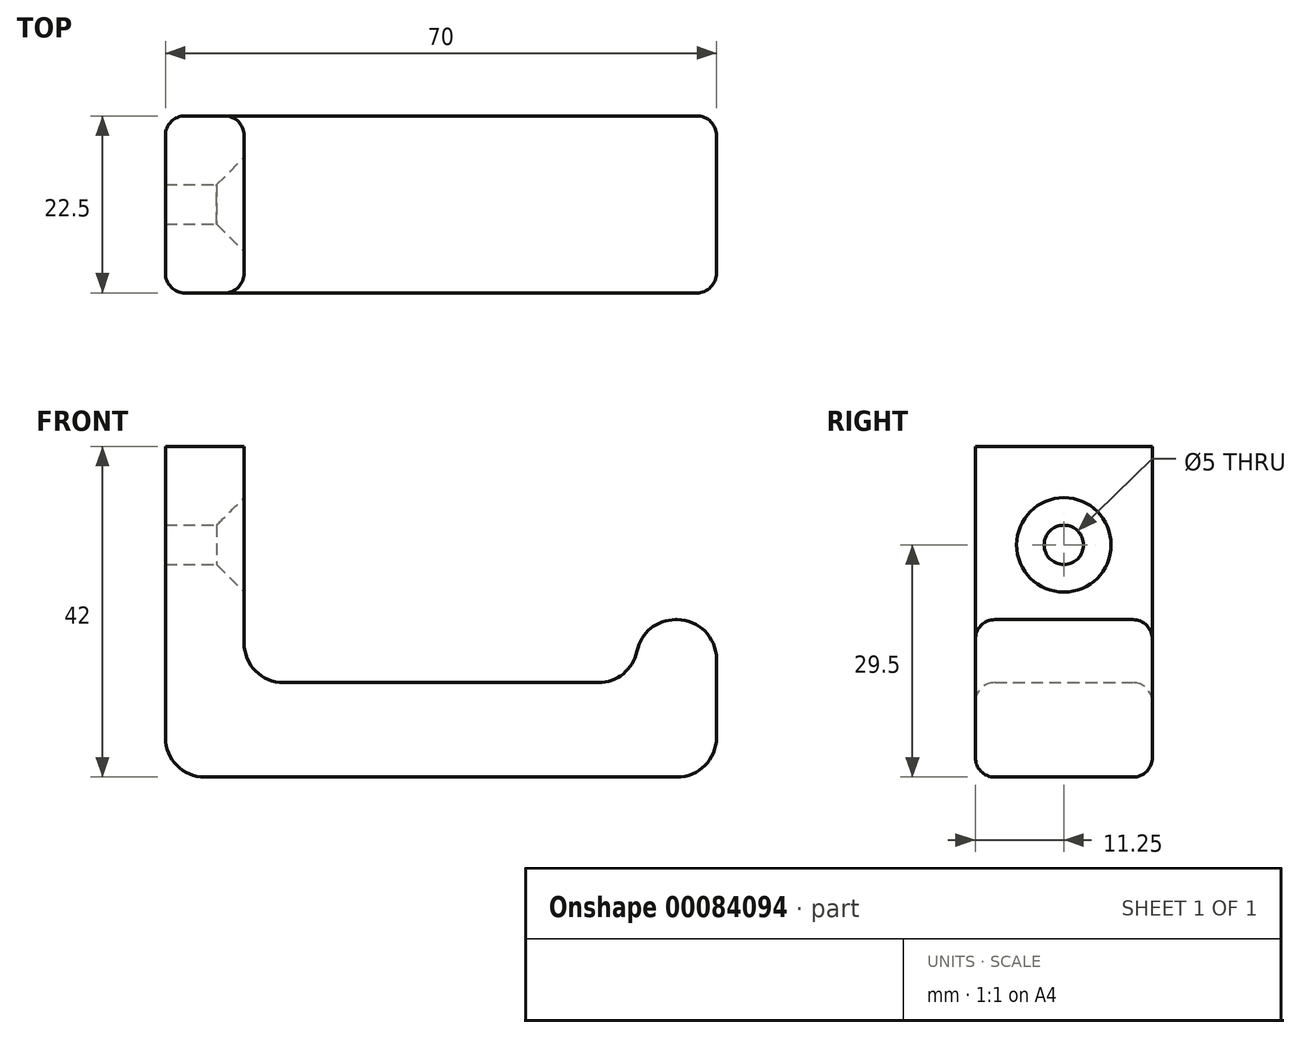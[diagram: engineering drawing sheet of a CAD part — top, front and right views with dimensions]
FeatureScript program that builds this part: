
annotation { "Feature Type Name" : "Feature", "Feature Type Description" : "" }
export const myFeature = defineFeature(function(context is Context, id is Id, definition is map)
    precondition{}
    {
        {
            var Q0;
            Q0=qCreatedBy(makeId("Front.planeOp"),FACE);
            var sketch = newSketch(context, id + "F0", { "sketchPlane" : qUnion([Q0])});
            skLineSegment(sketch, "E0", {"start": v(0, 5) * mm, "end": v(0, 42) * mm});
            skLineSegment(sketch, "E1", {"start": v(0, 42) * mm, "end": v(10, 42) * mm});
            skLineSegment(sketch, "E2", {"start": v(10, 42) * mm, "end": v(10, 17) * mm});
            skLineSegment(sketch, "E3", {"start": v(15, 12) * mm, "end": v(55, 12) * mm});
            skLineSegment(sketch, "E4", {"start": v(60, 17) * mm, "end": v(60, 20) * mm});
            skLineSegment(sketch, "E5", {"start": v(60, 20) * mm, "end": v(70, 20) * mm});
            skLineSegment(sketch, "E6", {"start": v(70, 20) * mm, "end": v(70, 5) * mm});
            skLineSegment(sketch, "E7", {"start": v(65, 0) * mm, "end": v(5, 0) * mm});
            skPoint(sketch, "E8.visualSharp", {"position": v(10, 12) * mm});
            skArc(sketch, "E8.filletArc", {"start": v(10, 17) * mm, "mid": v(11.46, 13.46) * mm, "end": v(15, 12) * mm});
            skPoint(sketch, "E9.visualSharp", {"position": v(60, 12) * mm});
            skArc(sketch, "E9.filletArc", {"start": v(55, 12) * mm, "mid": v(58.54, 13.46) * mm, "end": v(60, 17) * mm});
            skPoint(sketch, "E10.visualSharp", {"position": v(70, 0) * mm});
            skArc(sketch, "E10.filletArc", {"start": v(65, 0) * mm, "mid": v(68.54, 1.46) * mm, "end": v(70, 5) * mm});
            skPoint(sketch, "E11.visualSharp", {"position": v(0, 0) * mm});
            skArc(sketch, "E11.filletArc", {"start": v(0, 5) * mm, "mid": v(1.46, 1.46) * mm, "end": v(5, 0) * mm});
            skSolve(sketch);
        }
        {
            var Q0;
            Q0 = qSketchRegion(id + "F0", true);
            extrude(context, id + "F1", {"entities" : qUnion([Q0]), "depth" : 22.5 * mm});
        }
        {
            var Q0;
            Q0=makeQuery(id+"F1.opExtrude","SWEPT_FACE",FACE,{"disambiguationData":[OSD([sQuery(id+"F0.wireOp",EDGE,"E2")])]});
            var sketch = newSketch(context, id + "F2", { "sketchPlane" : qUnion([Q0])});
            skLineSegment(sketch, "E12", {"start": v(-22.5, 42) * mm, "end": v(0, 42) * mm});
            skLineSegment(sketch, "E13", {"start": v(-11.25, 42) * mm, "end": v(-11.25, 17) * mm});
            skPoint(sketch, "E13.endSnap0", {"position": v(-11.25, 42) * mm});
            skCircle(sketch, "E14", {"center": v(-11.25, 29.5) * mm, "radius": 2.5 * mm});
            skSolve(sketch);
        }
        {
            var Q0;
            {var subQ0=sQuery(id+"F2.wireOp",EDGE,"E14");var subQ1=sQuery(id+"F2.wireOp",EDGE,"E13");var subQ2=makeQuery(id+"F2.imprint","INTERSECT",VERTEX,{"disambiguationData":[OD(0.0)],"derivedFrom":[subQ1,subQ0]});Q0=makeQuery(id+"F2.imprint","IMPRINT",FACE,{"disambiguationData":[TD([[makeQuery(id+"F2.imprint","IMPRINT",EDGE,{"disambiguationData":[TD([[subQ2,-1.0]])],"derivedFrom":subQ1}),1.0]])]});}
            var Q1;
            {var subQ0=sQuery(id+"F2.wireOp",EDGE,"E14");var subQ1=sQuery(id+"F2.wireOp",EDGE,"E13");var subQ2=makeQuery(id+"F2.imprint","INTERSECT",VERTEX,{"disambiguationData":[OD(0.0)],"derivedFrom":[subQ1,subQ0]});Q1=makeQuery(id+"F2.imprint","IMPRINT",FACE,{"disambiguationData":[TD([[makeQuery(id+"F2.imprint","IMPRINT",EDGE,{"disambiguationData":[TD([[subQ2,-1.0]])],"derivedFrom":subQ1}),-1.0]])]});}
            extrude(context, id + "F3", {"entities" : qUnion([Q0, Q1]), "operationType" : NewBodyOperationType.REMOVE, "oppositeDirection" : true, "depth" : 25 * mm});
        }
        {
            var Q0;
            Q0=sQuery(id+"F2.wireOp",EDGE,"E13");
            cPlane(context, id + "F4", {"entities" : qUnion([Q0]), "cplaneType" : CPlaneType.LINE_ANGLE, "offset" : 150 * mm, "angle" : 90 * degree, "width" : 150 * mm, "height" : 150 * mm});
        }
        {
            var Q0;
            Q0=qCreatedBy(id+"F4.planeOp",FACE);
            var sketch = newSketch(context, id + "F5", { "sketchPlane" : qUnion([Q0])});
            skLineSegment(sketch, "E15", {"start": v(0, 42) * mm, "end": v(-10, 42) * mm});
            skLineSegment(sketch, "E16", {"start": v(-10, 42) * mm, "end": v(-10, 32) * mm});
            skLineSegment(sketch, "E17", {"start": v(-10, 32) * mm, "end": v(-6.5, 32) * mm});
            skLineSegment(sketch, "E18", {"start": v(-6.5, 32) * mm, "end": v(-10, 35.5) * mm});
            skLineSegment(sketch, "E19", {"start": v(-10, 29.5) * mm, "end": v(0, 29.5) * mm});
            skSolve(sketch);
        }
        {
            var Q0;
            Q0 = qSketchRegion(id + "F5", true);
            var Q1;
            Q1=sQuery(id+"F5.wireOp",EDGE,"E19");
            revolve(context, id + "F6", {"operationType" : NewBodyOperationType.REMOVE, "entities" : qUnion([Q0]), "axis" : qUnion([Q1]), "revolveType" : RevolveType.FULL, "oppositeDirection" : true});
        }
        {
            var Q0;
            Q0=makeQuery(id+"F1.opExtrude","SWEPT_EDGE",EDGE,{"disambiguationData":[OSD([sQuery(id+"F0.wireOp",EDGE,"E4"),sQuery(id+"F0.wireOp",EDGE,"E5")])]});
            fillet(context, id + "F7", {"entities" : qUnion([Q0]), "radius" : 5 * mm, "tangentPropagation" : true, "allowEdgeOverflow" : false});
        }
        {
            var Q0;
            Q0=makeQuery(id+"F1.opExtrude","SWEPT_EDGE",EDGE,{"disambiguationData":[OSD([sQuery(id+"F0.wireOp",EDGE,"E5"),sQuery(id+"F0.wireOp",EDGE,"E6")])]});
            fillet(context, id + "F8", {"entities" : qUnion([Q0]), "radius" : 5 * mm, "tangentPropagation" : true, "allowEdgeOverflow" : false});
        }
        {
            var Q0;
            Q0=makeQuery(id+"F1.opExtrude","CAP_EDGE",EDGE,{"disambiguationData":[OSD([sQuery(id+"F0.wireOp",EDGE,"E3")])],"isStart":true});
            var Q1;
            Q1=makeQuery(id+"F1.opExtrude","CAP_EDGE",EDGE,{"disambiguationData":[OSD([sQuery(id+"F0.wireOp",EDGE,"E3")])],"isStart":false});
            fillet(context, id + "F9", {"entities" : qUnion([Q0, Q1]), "radius" : 2.5 * mm, "tangentPropagation" : true, "allowEdgeOverflow" : false});
        }
    });
